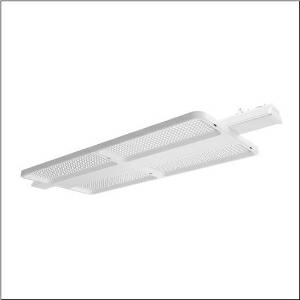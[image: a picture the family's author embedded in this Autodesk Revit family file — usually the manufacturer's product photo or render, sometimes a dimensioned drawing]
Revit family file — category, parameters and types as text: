
# Revit family: highbay_21_fur_licross_tragschiene_maxi_52hn11db4qla
name_source: partatom
category: Lighting Fixtures
units: mm (PartAtom-declared; Revit-internal decimal feet)

## family parameters
Cut with Voids When Loaded = No
Host = Face
Light Source = No
Part Type = Normal
Room Calculation Point = No
Round Connector Dimension = Use Diameter
Shared = No

## types (1)
- --- (1 x LED, 38000 lm, 197.7 W, 4000K)
    Apparent Load = 198 VA
    CIE Flux Codes = 89 97 99 100 100
    Color Rendering = 80
    Color Temperature = 4000K
    Default Elevation = 1800 mm
    Description = high bay luminaire Highbay 21 for Licross trunking rail maxi; direct symmetric narrow distribution, light control with lens of PMMA; UGR ≤ 22 (X = 4H | Y = 8H | S = 0.25H | reflection values 70/50/20); luminous flux: 38.000lm; light colour: 840, colour temperature: 4000K, MacAdam ≤ 3 SDCM (initial), colour rendering: CRI > 80; luminous efficacy: 192,2lm/W; rated service life: 75.000h (L80) at AT= ta max; control: DALI 2; luminaire connection: plug, 5-pole, with phase selectionmains connection: 230..240V, AC 50/60Hz; connected load: 197,7W; protection rating (complete): IP64; insulation class (complete): insulation class I (protective earthing); protection symbol: D; impact resistance: IK06; certification: CE, ENEC, VDE, UKCA; internal wiring halogen-free; luminaire LABS conformity tested according to VDMA 24364:2018-05; Suitable for use in the food industry according to the specifications of IFS-Food, HACCP and/or BRC; housing frame of high-performance plastic PA6, matt traffic white (RAL 9016); cover of PMMA; fixing on rail side of steel, galvanised, white; blank cover of PC/ABS, traffic white (RAL 9016); dimension (LxWxH): 1.250 x 442 x 71mm; permissible operating ambient temperature: -40..+55°C (reducing of maximum allowable ambient temperature of 5°C with ceiling mounting); packaging unit: 1 piece
    Height = 72 mm  [stored 0.23622 ft]
    Lamp = 1 x LED
    Lamp Light Flux = 38000 lm
    Lamp Power = 197.7 W
    Lamp count = 1
    Length = 946 mm
    Luminous efficacy = 192 lm/W
    Manufacturer = Siteco
    ModVariant = No
    Model = 52HN11DB4QLA
    Mounting Place = Ceiling
    Mounting Type = Pendant
    Number of Poles = 1
    OnlyDefault = Yes
    Power Factor = 1
    Product Name = Highbay 21 für Licross Tragschiene maxi
    Product group = high bay luminaire
    ProductGroupID = 902
    Protection Class = Protection class I
    Protection Degree = IP 64
    RLX_Detail_Level = 1
    RLX_Emergency_Light_Flux = 0 lm
    RLX_Emergency_Type = 0
    RLX_Emergency_Type_DB = No
    RlxData = <blob elided: 129829 chars, md5=6786ad6b>
    Socket = socket
    Standby Power = 0 W
    System Light Flux = 38000 lm
    System Power = 198 W
    Type Comments = factory setting: luminous flux: 100 % | dim-lin: 254 | 918 mA
    Type Image = l_1361711.jpg
    URL = http://relux.com
    VarID = @adj_015943
    Voltage = 0 V
    Weight = 0.00 kg
    Width = 442 mm

note: [stored X ft] marks values corroborated as IEEE doubles in the binary element streams (Revit-internal decimal feet)

## geometry (parser evidence)
native form markers: Blend x4, Sweep x10
no freeform markers — native parametric forms only
